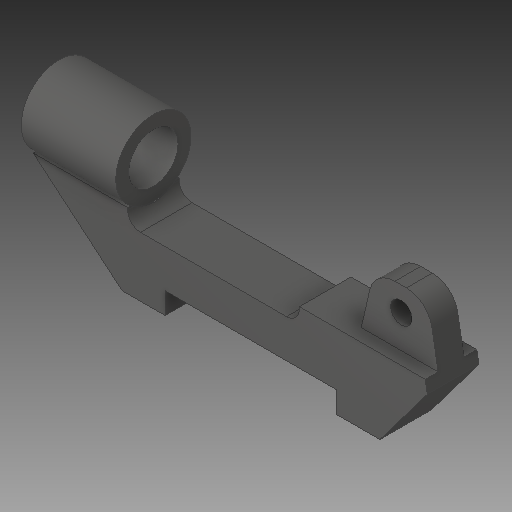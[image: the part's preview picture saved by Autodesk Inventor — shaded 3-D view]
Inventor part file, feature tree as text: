
AUTODESK INVENTOR PART (.ipt)
format: ipt  version: 2019 (Build 230136000, 136)  size: 130,560 bytes
history: mixed  units: in
note: dims shown in document units (in); Inventor stores cm internally (conversion verified against a paired STEP export)
features: other x1, extrude x1, imported_body x1
ambient origin geometry x8: Origin, YZ Plane, XZ Plane, XY Plane, X Axis, Y Axis, Z Axis, Center Point
bodies: Solid1 (imported_parasolid), Solid2 (imported_parasolid)
feature tree (3):
  other  "Cut-Extrude1"
  extrude  "Extrude-Thin4"  [1 undecoded]
  imported_body  NMx_Import_Brep_tag  [imported B-rep: ~12 faces, bbox_mm=[22.0, 7.5, 14.75]]
note: 1 required parameter value undecoded (feature->parameter linkage not recoverable at this tier; creation-order binding heuristic only, values carry confidence <= 0.55)
